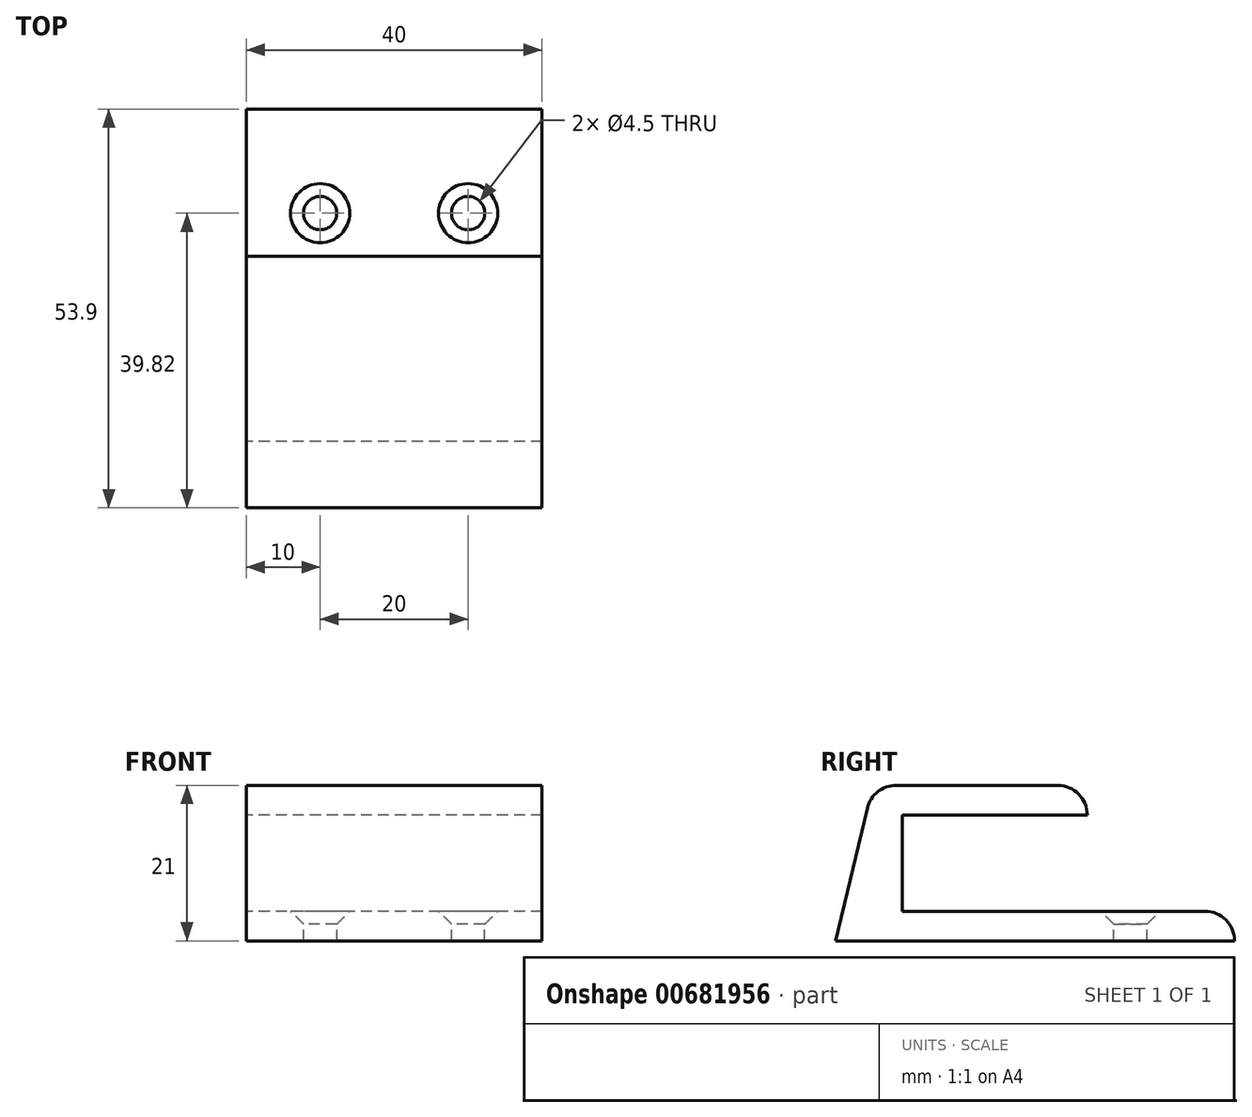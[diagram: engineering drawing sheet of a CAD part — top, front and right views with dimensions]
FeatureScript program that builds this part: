
annotation { "Feature Type Name" : "Feature", "Feature Type Description" : "" }
export const myFeature = defineFeature(function(context is Context, id is Id, definition is map)
    precondition{}
    {
        {
            var Q0;
            Q0=qCreatedBy(makeId("Right.planeOp"),FACE);
            var sketch = newSketch(context, id + "F0", { "sketchPlane" : qUnion([Q0])});
            skLineSegment(sketch, "E0.bottom", {"start": v(-17.45, 16.5) * mm, "end": v(22.95, 16.5) * mm});
            skLineSegment(sketch, "E0.top", {"start": v(-17.45, 4.5) * mm, "end": v(22.95, 4.5) * mm});
            skLineSegment(sketch, "E0.left", {"start": v(-17.45, 16.5) * mm, "end": v(-17.45, 4.5) * mm});
            skLineSegment(sketch, "E0.right", {"start": v(22.95, 16.5) * mm, "end": v(22.95, 4.5) * mm});
            skLineSegment(sketch, "E1", {"start": v(22.95, 4) * mm, "end": v(-17.95, 4) * mm});
            skLineSegment(sketch, "E2", {"start": v(-17.95, 4) * mm, "end": v(-17.95, 17) * mm});
            skLineSegment(sketch, "E3", {"start": v(-17.95, 17) * mm, "end": v(7.05, 17) * mm});
            skLineSegment(sketch, "E4", {"start": v(3.05, 21) * mm, "end": v(-18.8, 21) * mm});
            skLineSegment(sketch, "E5", {"start": v(-21.95, 21) * mm, "end": v(-21.95, 0) * mm, "construction": true});
            skLineSegment(sketch, "E6", {"start": v(-26.95, 0) * mm, "end": v(26.95, 0) * mm});
            skArc(sketch, "E7", {"start": v(-21.95, 4) * mm, "mid": v(-20.78, 1.17) * mm, "end": v(-17.95, 0) * mm, "construction": true});
            skArc(sketch, "E8", {"start": v(-17.95, 21) * mm, "mid": v(-20.78, 19.83) * mm, "end": v(-21.95, 17) * mm, "construction": true});
            skArc(sketch, "E9", {"start": v(-17.45, 17) * mm, "mid": v(-17.8, 16.85) * mm, "end": v(-17.95, 16.5) * mm, "construction": true});
            skArc(sketch, "E10", {"start": v(-17.95, 4.5) * mm, "mid": v(-17.8, 4.15) * mm, "end": v(-17.45, 4) * mm, "construction": true});
            skArc(sketch, "E11", {"start": v(26.95, 0) * mm, "mid": v(25.78, 2.83) * mm, "end": v(22.95, 4) * mm});
            skArc(sketch, "E12", {"start": v(7.05, 17) * mm, "mid": v(5.88, 19.83) * mm, "end": v(3.05, 21) * mm});
            skLineSegment(sketch, "E13", {"start": v(-22.68, 17.93) * mm, "end": v(-26.95, 0) * mm});
            skPoint(sketch, "E14.visualSharp", {"position": v(-21.95, 21) * mm});
            skArc(sketch, "E14.filletArc", {"start": v(-18.8, 21) * mm, "mid": v(-21.27, 20.14) * mm, "end": v(-22.68, 17.93) * mm});
            skLineSegment(sketch, "E15", {"start": v(-7.87, 21) * mm, "end": v(-7.87, 0) * mm, "construction": true});
            skLineSegment(sketch, "E16", {"start": v(12.87, 0) * mm, "end": v(12.87, 4) * mm, "construction": true});
            skLineSegment(sketch, "E17", {"start": v(-17.95, 4) * mm, "end": v(-7.87, 0) * mm, "construction": true});
            skLineSegment(sketch, "E18", {"start": v(12.87, 0) * mm, "end": v(22.95, 4) * mm, "construction": true});
            skSolve(sketch);
        }
        {
            var Q0;
            Q0=makeQuery(id+"F0.imprint","IMPRINT",FACE,{"disambiguationData":[TD([[makeQuery(id+"F0.imprint","IMPRINT",EDGE,{"derivedFrom":sQuery(id+"F0.wireOp",EDGE,"E1")}),1.0]])]});
            extrude(context, id + "F1", {"entities" : qUnion([Q0]), "endBound" : BoundingType.SYMMETRIC, "depth" : 40 * mm, "offsetDistance" : 25 * mm});
        }
        {
            var Q0;
            Q0=makeQuery(id+"F1.opExtrude","SWEPT_FACE",FACE,{"disambiguationData":[OSD([sQuery(id+"F0.wireOp",EDGE,"E1")])]});
            var sketch = newSketch(context, id + "F2", { "sketchPlane" : qUnion([Q0])});
            skLineSegment(sketch, "E19", {"start": v(10, 12.87) * mm, "end": v(0, 12.87) * mm, "construction": true});
            skPoint(sketch, "E20", {"position": v(0, -7.87) * mm});
            skLineSegment(sketch, "E21", {"start": v(-10, 12.87) * mm, "end": v(-20, 12.87) * mm, "construction": true});
            skLineSegment(sketch, "E22", {"start": v(10, 12.87) * mm, "end": v(20, 12.87) * mm, "construction": true});
            skLineSegment(sketch, "E23", {"start": v(0, 12.87) * mm, "end": v(-10, 12.87) * mm, "construction": true});
            skSolve(sketch);
        }
        {
            var Q0;
            Q0=sQuery(id+"F2.wireOp",VERTEX,"E21.start");
            var Q1;
            Q1=sQuery(id+"F2.wireOp",VERTEX,"E19.start");
            var Q2;
            Q2=makeQuery(id+"F1.opExtrude","SWEPT_BODY",BODY,{"disambiguationData":[OSD([sQuery(id+"F0.wireOp",EDGE,"E1"),sQuery(id+"F0.wireOp",EDGE,"E2"),sQuery(id+"F0.wireOp",EDGE,"E3"),sQuery(id+"F0.wireOp",EDGE,"E4"),sQuery(id+"F0.wireOp",EDGE,"E6"),sQuery(id+"F0.wireOp",EDGE,"E11"),sQuery(id+"F0.wireOp",EDGE,"E12"),sQuery(id+"F0.wireOp",EDGE,"E13"),sQuery(id+"F0.wireOp",EDGE,"E14.filletArc")])]});
            hole(context, id + "F3", {"style" : HoleStyle.C_SINK, "endStyle" : HoleEndStyle.THROUGH, "holeDiameter" : 4.5 * mm, "cSinkDiameter" : 8 * mm, "cSinkAngle" : 90 * degree, "majorDiameter" : 5 * mm, "isTappedThrough" : true, "tappedDepth" : 12 * mm, "tapClearance" : 3, "startFromSketch" : true, "locations" : qUnion([Q0, Q1]), "scope" : qUnion([Q2])});
        }
    });
